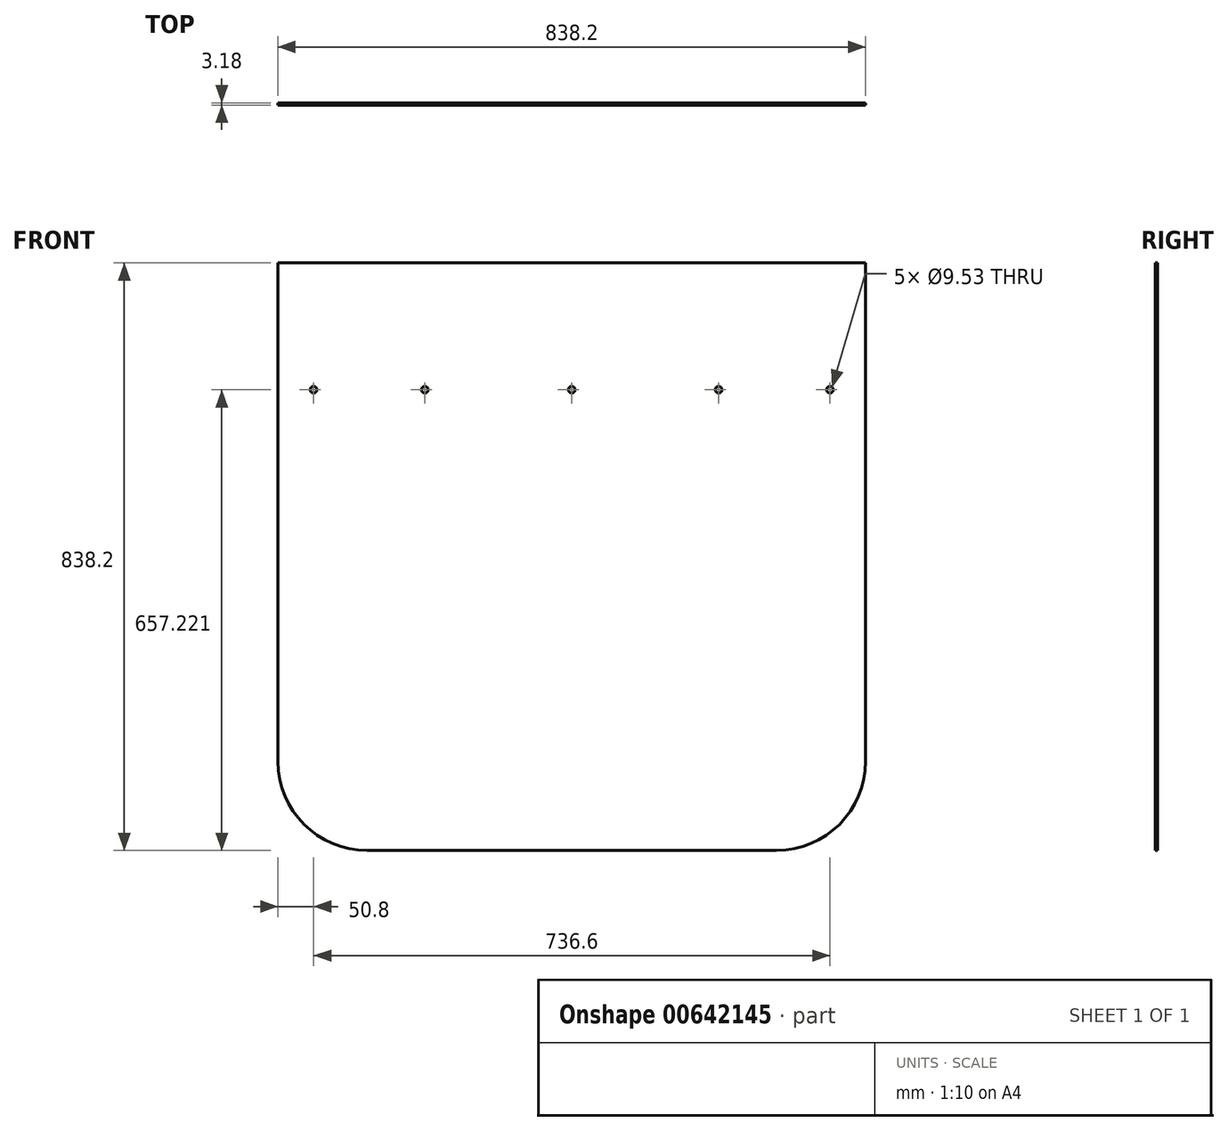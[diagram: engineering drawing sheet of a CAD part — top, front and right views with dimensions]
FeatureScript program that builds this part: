
annotation { "Feature Type Name" : "Feature", "Feature Type Description" : "" }
export const myFeature = defineFeature(function(context is Context, id is Id, definition is map)
    precondition{}
    {
        {
            var Q0;
            Q0=qCreatedBy(makeId("Front.planeOp"),FACE);
            var sketch = newSketch(context, id + "F0", { "sketchPlane" : qUnion([Q0])});
            skLineSegment(sketch, "E0", {"start": v(-56.44, 859.48) * mm, "end": v(-56.44, 148.28) * mm});
            skLineSegment(sketch, "E1", {"start": v(-56.44, 859.48) * mm, "end": v(781.76, 859.48) * mm});
            skLineSegment(sketch, "E2", {"start": v(781.76, 859.48) * mm, "end": v(781.76, 148.28) * mm});
            skLineSegment(sketch, "E3", {"start": v(654.76, 21.28) * mm, "end": v(70.56, 21.28) * mm});
            skPoint(sketch, "E4.visualSharp", {"position": v(-56.44, 21.28) * mm});
            skArc(sketch, "E4.filletArc", {"start": v(-56.44, 148.28) * mm, "mid": v(-19.24, 58.47) * mm, "end": v(70.56, 21.28) * mm});
            skPoint(sketch, "E5.visualSharp", {"position": v(781.76, 21.28) * mm});
            skArc(sketch, "E5.filletArc", {"start": v(654.76, 21.28) * mm, "mid": v(744.56, 58.47) * mm, "end": v(781.76, 148.28) * mm});
            skCircle(sketch, "E6", {"center": v(362.66, 678.5) * mm, "radius": 4.76 * mm});
            skCircle(sketch, "E7", {"center": v(153.1, 678.5) * mm, "radius": 4.76 * mm});
            skCircle(sketch, "E8", {"center": v(572.2, 678.5) * mm, "radius": 4.76 * mm});
            skCircle(sketch, "E9", {"center": v(730.96, 678.5) * mm, "radius": 4.76 * mm});
            skCircle(sketch, "E10", {"center": v(-5.64, 678.5) * mm, "radius": 4.76 * mm});
            skSolve(sketch);
        }
        {
            var Q0;
            Q0=makeQuery(id+"F0.imprint","IMPRINT",FACE,{"disambiguationData":[TD([[makeQuery(id+"F0.imprint","IMPRINT",EDGE,{"derivedFrom":sQuery(id+"F0.wireOp",EDGE,"E0")}),1.0]])]});
            extrude(context, id + "F1", {"entities" : qUnion([Q0]), "depth" : 3.17 * mm, "offsetDistance" : 25.4 * mm});
        }
    });
